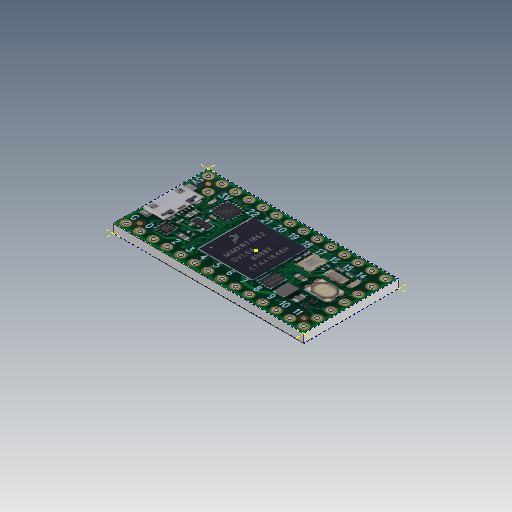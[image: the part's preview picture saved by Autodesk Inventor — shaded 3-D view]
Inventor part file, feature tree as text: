
AUTODESK INVENTOR PART (.ipt)
format: ipt  version: 2020 (Build 240168000, 168)  size: 939,520 bytes
history: native  units: in
note: dims shown in document units (in); Inventor stores cm internally (conversion verified against a paired STEP export)
features: other x3, sketch x2
ambient origin geometry x8: Origin, YZ Plane, XZ Plane, XY Plane, X Axis, Y Axis, Z Axis, Center Point
bodies: Solid1 (feature_tree)
feature tree (5):
  other  "Boss-Extrude1"
  sketch  "Sketch1"
  sketch  "Sketch2"
  other  "Image1"
  other  "Image2"
